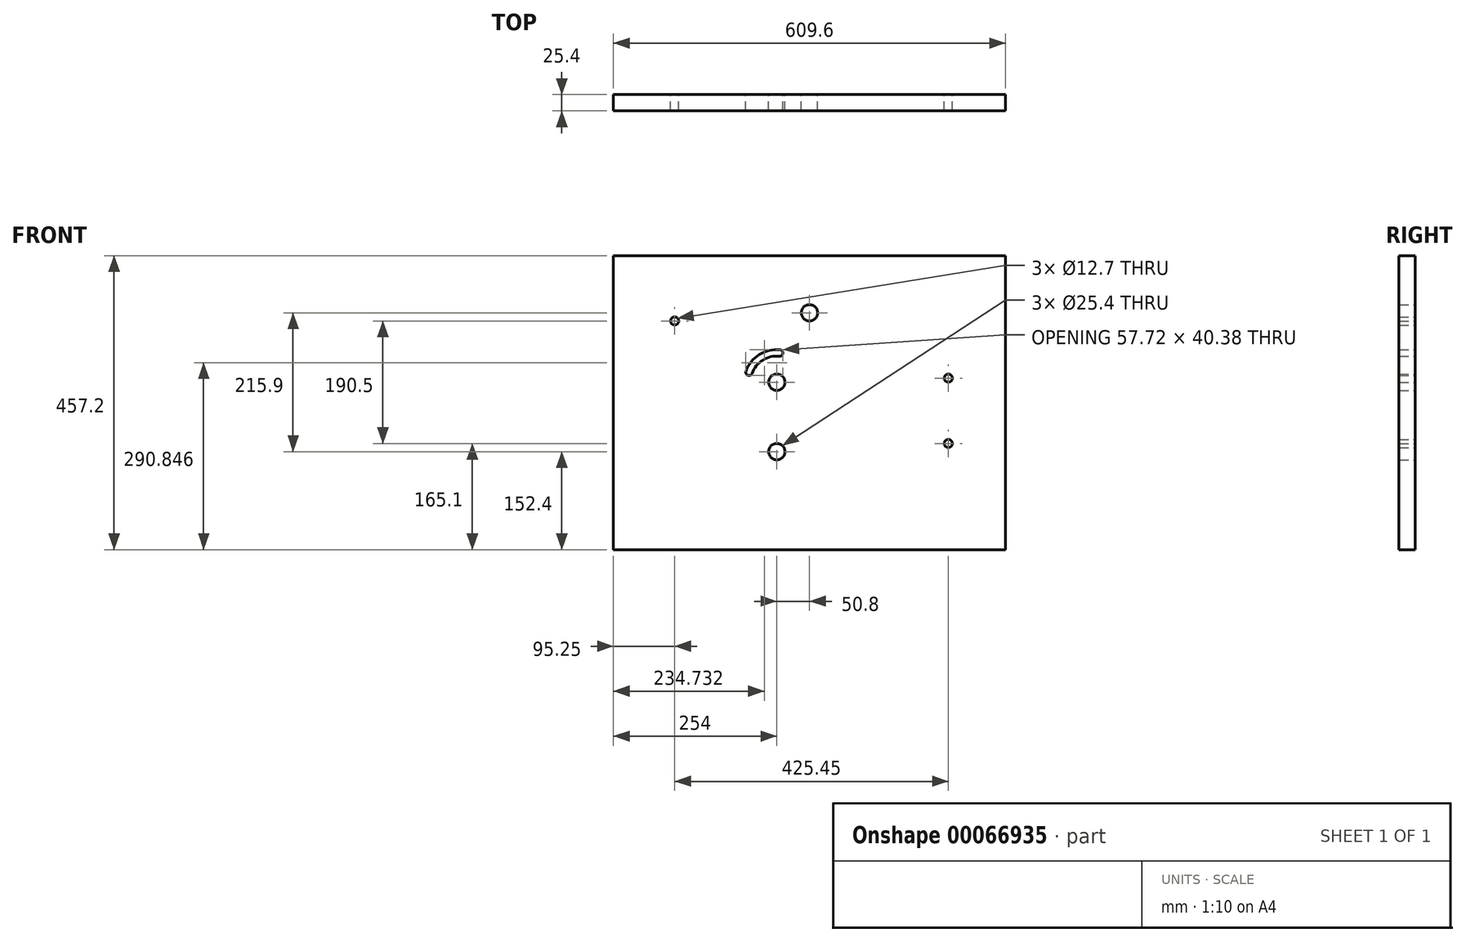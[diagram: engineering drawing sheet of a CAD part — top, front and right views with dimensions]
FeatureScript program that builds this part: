
annotation { "Feature Type Name" : "Feature", "Feature Type Description" : "" }
export const myFeature = defineFeature(function(context is Context, id is Id, definition is map)
    precondition{}
    {
        {
            var Q0;
            Q0=qCreatedBy(makeId("Front.planeOp"),FACE);
            var sketch = newSketch(context, id + "F0", { "sketchPlane" : qUnion([Q0])});
            skLineSegment(sketch, "E0.bottom", {"start": v(0, 0) * mm, "end": v(609.6, 0) * mm});
            skLineSegment(sketch, "E0.top", {"start": v(0, 457.2) * mm, "end": v(609.6, 457.2) * mm});
            skLineSegment(sketch, "E0.left", {"start": v(0, 0) * mm, "end": v(0, 457.2) * mm});
            skLineSegment(sketch, "E0.right", {"start": v(609.6, 0) * mm, "end": v(609.6, 457.2) * mm});
            skCircle(sketch, "E1", {"center": v(95.25, 355.6) * mm, "radius": 6.35 * mm});
            skCircle(sketch, "E2", {"center": v(254, 152.4) * mm, "radius": 12.7 * mm});
            skCircle(sketch, "E3", {"center": v(254, 260.35) * mm, "radius": 12.7 * mm});
            skCircle(sketch, "E4", {"center": v(304.8, 368.3) * mm, "radius": 12.7 * mm});
            skCircle(sketch, "E5", {"center": v(520.7, 266.7) * mm, "radius": 6.35 * mm});
            skCircle(sketch, "E6", {"center": v(520.7, 165.1) * mm, "radius": 6.35 * mm});
            skLineSegment(sketch, "E7", {"start": v(254, 152.4) * mm, "end": v(254, 260.35) * mm, "construction": true});
            skCircle(sketch, "E8", {"center": v(254, 260.35) * mm, "radius": 45.72 * mm, "construction": true});
            skArc(sketch, "E9", {"start": v(259.04, 310.9) * mm, "mid": v(226.84, 303.28) * mm, "end": v(206.16, 277.44) * mm});
            skArc(sketch, "E10", {"start": v(206.16, 277.44) * mm, "mid": v(209.24, 270.94) * mm, "end": v(215.73, 274.02) * mm});
            skLineSegment(sketch, "E11", {"start": v(206.16, 277.44) * mm, "end": v(254, 260.35) * mm, "construction": true});
            skArc(sketch, "E12", {"start": v(258.03, 300.79) * mm, "mid": v(263.6, 305.34) * mm, "end": v(259.04, 310.9) * mm});
            skLineSegment(sketch, "E13", {"start": v(254, 260.35) * mm, "end": v(259.04, 310.9) * mm, "construction": true});
            skArc(sketch, "E14", {"start": v(258.03, 300.79) * mm, "mid": v(232.27, 294.7) * mm, "end": v(215.73, 274.02) * mm});
            skSolve(sketch);
        }
        {
            var Q0;
            Q0=makeQuery(id+"F0.imprint","IMPRINT",FACE,{"disambiguationData":[TD([[makeQuery(id+"F0.imprint","IMPRINT",EDGE,{"derivedFrom":sQuery(id+"F0.wireOp",EDGE,"E0.bottom")}),1.0]])]});
            extrude(context, id + "F1", {"entities" : qUnion([Q0]), "depth" : 25.4 * mm});
        }
    });
